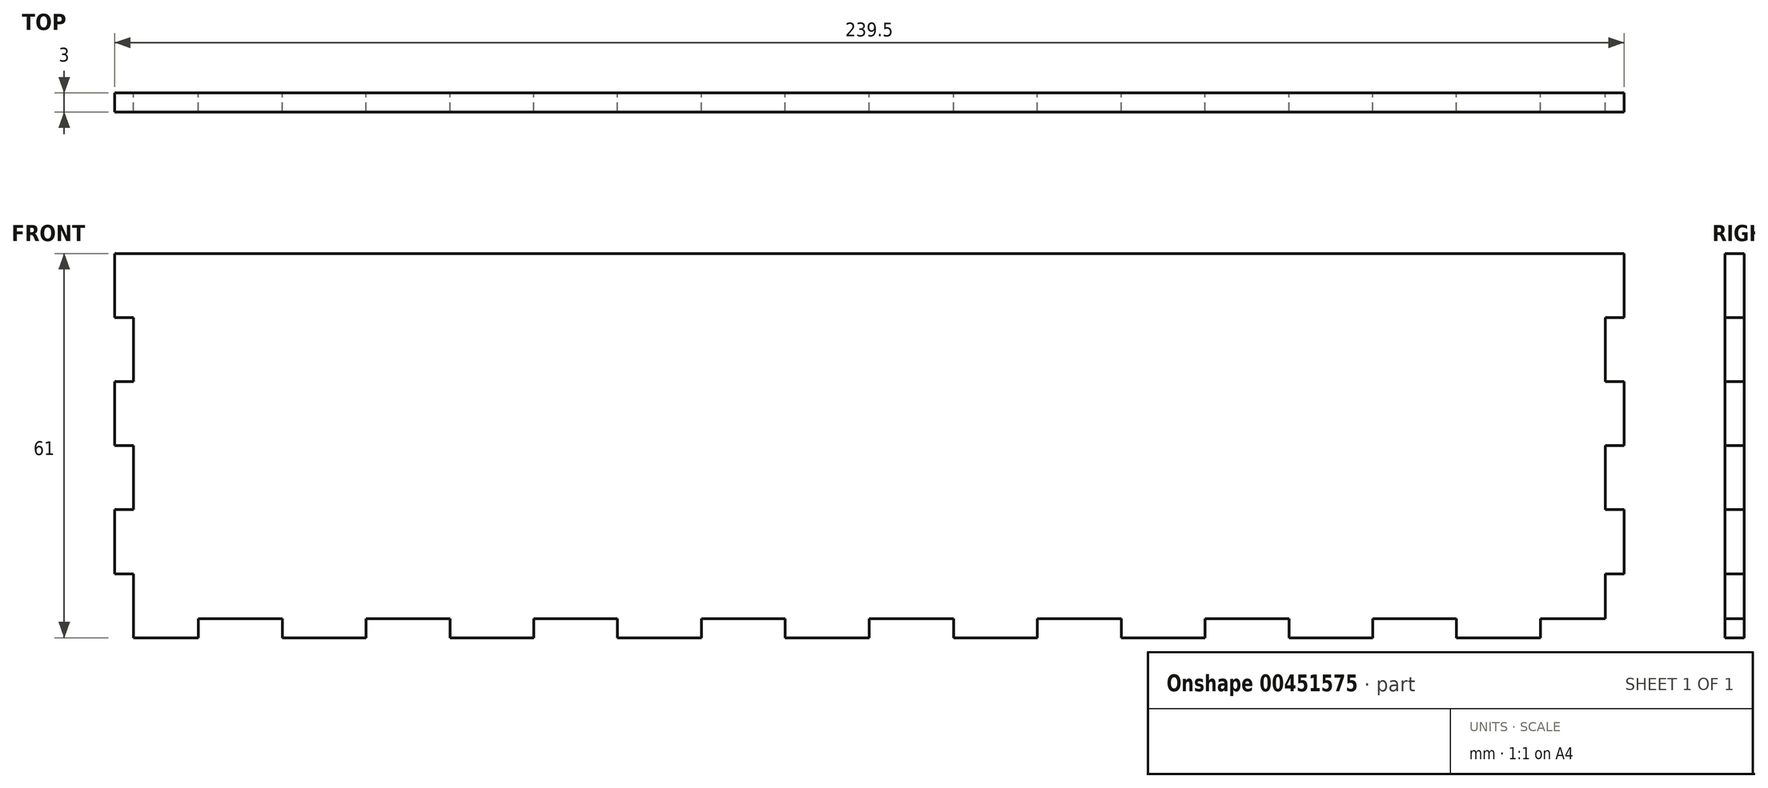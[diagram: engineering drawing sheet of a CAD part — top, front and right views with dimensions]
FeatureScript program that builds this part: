
annotation { "Feature Type Name" : "Feature", "Feature Type Description" : "" }
export const myFeature = defineFeature(function(context is Context, id is Id, definition is map)
    precondition{}
    {
        {
            var Q0;
            Q0=qCreatedBy(makeId("Front.planeOp"),FACE);
            var sketch = newSketch(context, id + "F0", { "sketchPlane" : qUnion([Q0])});
            skLineSegment(sketch, "E0.bottom", {"start": v(106.45, -13.52) * mm, "end": v(93.15, -13.52) * mm});
            skLineSegment(sketch, "E0.top", {"start": v(119.75, 47.48) * mm, "end": v(-119.75, 47.48) * mm});
            skLineSegment(sketch, "E0.right", {"start": v(-119.75, -3.35) * mm, "end": v(-119.75, 6.81) * mm});
            skLineSegment(sketch, "E1.MirrorCS", {"start": v(-0.05, -13.52) * mm, "end": v(-0.05, -10.52) * mm});
            skLineSegment(sketch, "E2.MirrorCS", {"start": v(0.05, -13.52) * mm, "end": v(0.05, -10.52) * mm});
            skLineSegment(sketch, "E3.MirrorCS", {"start": v(-66.55, -13.52) * mm, "end": v(-66.55, -10.52) * mm});
            skLineSegment(sketch, "E4.MirrorCS", {"start": v(-79.85, -13.52) * mm, "end": v(-79.85, -10.52) * mm});
            skLineSegment(sketch, "E5.MirrorCS", {"start": v(-93.15, -13.52) * mm, "end": v(-93.15, -10.52) * mm});
            skLineSegment(sketch, "E6.MirrorCS", {"start": v(-106.45, -13.52) * mm, "end": v(-106.45, -10.52) * mm});
            skLineSegment(sketch, "E7.MirrorCS", {"start": v(-39.95, -13.52) * mm, "end": v(-39.95, -10.52) * mm});
            skLineSegment(sketch, "E8.MirrorCS", {"start": v(-26.65, -13.52) * mm, "end": v(-26.65, -10.52) * mm});
            skLineSegment(sketch, "E9.MirrorCS", {"start": v(-13.35, -13.52) * mm, "end": v(-13.35, -10.52) * mm});
            skLineSegment(sketch, "E10.MirrorCS", {"start": v(53.25, -13.52) * mm, "end": v(53.25, -10.52) * mm});
            skLineSegment(sketch, "E11.MirrorCS", {"start": v(93.15, -13.52) * mm, "end": v(93.15, -10.52) * mm});
            skLineSegment(sketch, "E12.MirrorCS", {"start": v(106.45, -13.52) * mm, "end": v(106.45, -10.52) * mm});
            skLineSegment(sketch, "E13.MirrorCS", {"start": v(39.95, -13.52) * mm, "end": v(39.95, -10.52) * mm});
            skLineSegment(sketch, "E14.MirrorCS", {"start": v(79.85, -13.52) * mm, "end": v(79.85, -10.52) * mm});
            skLineSegment(sketch, "E15.MirrorCS", {"start": v(26.65, -13.52) * mm, "end": v(26.65, -10.52) * mm});
            skLineSegment(sketch, "E16.MirrorCS", {"start": v(66.55, -13.52) * mm, "end": v(66.55, -10.52) * mm});
            skLineSegment(sketch, "E17.MirrorCS", {"start": v(13.35, -13.52) * mm, "end": v(13.35, -10.52) * mm});
            skLineSegment(sketch, "E18.MirrorCS", {"start": v(-53.25, -13.52) * mm, "end": v(-53.25, -10.52) * mm});
            skLineSegment(sketch, "E19.MirrorCS", {"start": v(-106.45, -10.52) * mm, "end": v(-93.15, -10.52) * mm});
            skLineSegment(sketch, "E20.trimOffspring", {"start": v(-106.45, -13.52) * mm, "end": v(-116.75, -13.52) * mm});
            skLineSegment(sketch, "E21.trimOffspring", {"start": v(-79.85, -10.52) * mm, "end": v(-66.55, -10.52) * mm});
            skLineSegment(sketch, "E22.trimOffspring", {"start": v(-79.85, -13.52) * mm, "end": v(-93.15, -13.52) * mm});
            skLineSegment(sketch, "E23.trimOffspring", {"start": v(-53.25, -10.52) * mm, "end": v(-39.95, -10.52) * mm});
            skLineSegment(sketch, "E24.trimOffspring", {"start": v(-53.25, -13.52) * mm, "end": v(-66.55, -13.52) * mm});
            skLineSegment(sketch, "E25.trimOffspring", {"start": v(-26.65, -10.52) * mm, "end": v(-13.35, -10.52) * mm});
            skLineSegment(sketch, "E26.trimOffspring", {"start": v(-26.65, -13.52) * mm, "end": v(-39.95, -13.52) * mm});
            skLineSegment(sketch, "E27.trimOffspring", {"start": v(-0.05, -10.52) * mm, "end": v(13.35, -10.52) * mm});
            skLineSegment(sketch, "E28.trimOffspring", {"start": v(0.05, -13.52) * mm, "end": v(-0.05, -13.52) * mm});
            skLineSegment(sketch, "E29.trimOffspring", {"start": v(0.05, -13.52) * mm, "end": v(-13.35, -13.52) * mm});
            skLineSegment(sketch, "E30.trimOffspring", {"start": v(26.65, -10.52) * mm, "end": v(39.95, -10.52) * mm});
            skLineSegment(sketch, "E31.trimOffspring", {"start": v(26.65, -13.52) * mm, "end": v(13.35, -13.52) * mm});
            skLineSegment(sketch, "E32.trimOffspring", {"start": v(53.25, -10.52) * mm, "end": v(66.55, -10.52) * mm});
            skLineSegment(sketch, "E33.trimOffspring", {"start": v(53.25, -13.52) * mm, "end": v(39.95, -13.52) * mm});
            skLineSegment(sketch, "E34.trimOffspring", {"start": v(79.85, -10.52) * mm, "end": v(93.15, -10.52) * mm});
            skLineSegment(sketch, "E35.trimOffspring", {"start": v(79.85, -13.52) * mm, "end": v(66.55, -13.52) * mm});
            skLineSegment(sketch, "E36.trimOffspring", {"start": v(106.45, -10.52) * mm, "end": v(116.75, -10.52) * mm});
            skLineSegment(sketch, "E37", {"start": v(-116.75, -13.52) * mm, "end": v(-116.75, -3.35) * mm});
            skLineSegment(sketch, "E38", {"start": v(-119.75, 37.31) * mm, "end": v(-116.75, 37.31) * mm});
            skLineSegment(sketch, "E39", {"start": v(-116.75, 27.15) * mm, "end": v(-119.75, 27.15) * mm});
            skLineSegment(sketch, "E40", {"start": v(-119.75, 16.98) * mm, "end": v(-116.75, 16.98) * mm});
            skLineSegment(sketch, "E41", {"start": v(-116.75, 16.98) * mm, "end": v(-116.75, 6.81) * mm});
            skLineSegment(sketch, "E42", {"start": v(-116.75, 6.81) * mm, "end": v(-119.75, 6.81) * mm});
            skLineSegment(sketch, "E43", {"start": v(-119.75, -3.35) * mm, "end": v(-116.75, -3.35) * mm});
            skLineSegment(sketch, "E44.trimOffspring", {"start": v(-119.75, 37.31) * mm, "end": v(-119.75, 47.48) * mm});
            skLineSegment(sketch, "E45.trimOffspring", {"start": v(-116.75, 27.15) * mm, "end": v(-116.75, 37.31) * mm});
            skLineSegment(sketch, "E46.trimOffspring", {"start": v(-119.75, 16.98) * mm, "end": v(-119.75, 27.15) * mm});
            skLineSegment(sketch, "E47.trimOffspring", {"start": v(-116.75, 6.81) * mm, "end": v(-116.75, 16.98) * mm});
            skLineSegment(sketch, "E48.MirrorCS", {"start": v(116.75, 16.98) * mm, "end": v(116.75, 6.81) * mm});
            skLineSegment(sketch, "E49.MirrorCS", {"start": v(116.75, 6.81) * mm, "end": v(116.75, 16.98) * mm});
            skLineSegment(sketch, "E50.MirrorCS", {"start": v(119.75, 16.98) * mm, "end": v(119.75, 27.15) * mm});
            skLineSegment(sketch, "E51.MirrorCS", {"start": v(116.75, 6.81) * mm, "end": v(119.75, 6.81) * mm});
            skLineSegment(sketch, "E52.MirrorCS", {"start": v(116.75, 27.15) * mm, "end": v(119.75, 27.15) * mm});
            skLineSegment(sketch, "E53.MirrorCS", {"start": v(119.75, 37.31) * mm, "end": v(119.75, 47.48) * mm});
            skLineSegment(sketch, "E54.MirrorCS", {"start": v(119.75, 37.31) * mm, "end": v(116.75, 37.31) * mm});
            skLineSegment(sketch, "E55.MirrorCS", {"start": v(119.75, 16.98) * mm, "end": v(116.75, 16.98) * mm});
            skLineSegment(sketch, "E56.MirrorCS", {"start": v(116.75, 27.15) * mm, "end": v(116.75, 37.31) * mm});
            skLineSegment(sketch, "E57.MirrorCS", {"start": v(116.75, -10.52) * mm, "end": v(116.75, -3.35) * mm});
            skLineSegment(sketch, "E58.MirrorCS", {"start": v(119.75, -3.35) * mm, "end": v(119.75, 6.81) * mm});
            skLineSegment(sketch, "E59.MirrorCS", {"start": v(119.75, -3.35) * mm, "end": v(116.75, -3.35) * mm});
            skSolve(sketch);
        }
        {
            var Q0;
            Q0=makeQuery(id+"F0.imprint","IMPRINT",FACE,{"disambiguationData":[TD([[makeQuery(id+"F0.imprint","IMPRINT",EDGE,{"derivedFrom":sQuery(id+"F0.wireOp",EDGE,"E0.bottom")}),-1.0]])]});
            extrude(context, id + "F1", {"entities" : qUnion([Q0]), "depth" : 3 * mm, "offsetDistance" : 25 * mm});
        }
    });
